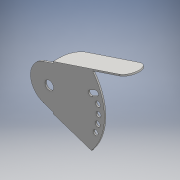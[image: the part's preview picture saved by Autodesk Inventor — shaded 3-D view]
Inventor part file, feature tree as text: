
AUTODESK INVENTOR PART (.ipt)
format: ipt  version: 2016 (Build 200138000, 138)  size: 182,784 bytes
history: native  units: mm
features: fillet x5, extrude x4, sketch x4
ambient origin geometry x8: Origin, YZ Plane, XZ Plane, XY Plane, X Axis, Y Axis, Z Axis, Center Point
bodies: Solid1 (feature_tree)
feature tree (13):
  extrude  "Extrusion1"  Depth=1.0mm
  extrude  "Extrusion2"  Depth=1.0mm TaperAngle=0.0deg
  fillet  "Fillet1"  Radius=6.999mm
  fillet  "Fillet2"  Radius=0.5mm
  extrude  "Extrusion3"  Depth=14.0mm
  fillet  "Fillet3"  Radius=1.0mm
  fillet  "Fillet4"  Radius=0.5mm
  fillet  "Fillet5"  Radius=0.5mm
  extrude  "Extrusion4"  Depth=1.0mm TaperAngle=0.0deg
  sketch  "Sketch1"  dims[d25=1.0mm d26=0.0mm d27=28.0mm]
  sketch  "Sketch2"  dims[d28=7.0mm d29=1.0mm d30=0.0mm d31=6.999mm d32=0.5mm]
  sketch  "Sketch4"  dims[d33=55.0mm d34=14.0mm d35=1.0mm d36=0.0mm d37=0.5mm d38=0.5mm]
  sketch  "Sketch5"  dims[d39=9.0mm d42=1.0mm d43=0.0mm]
